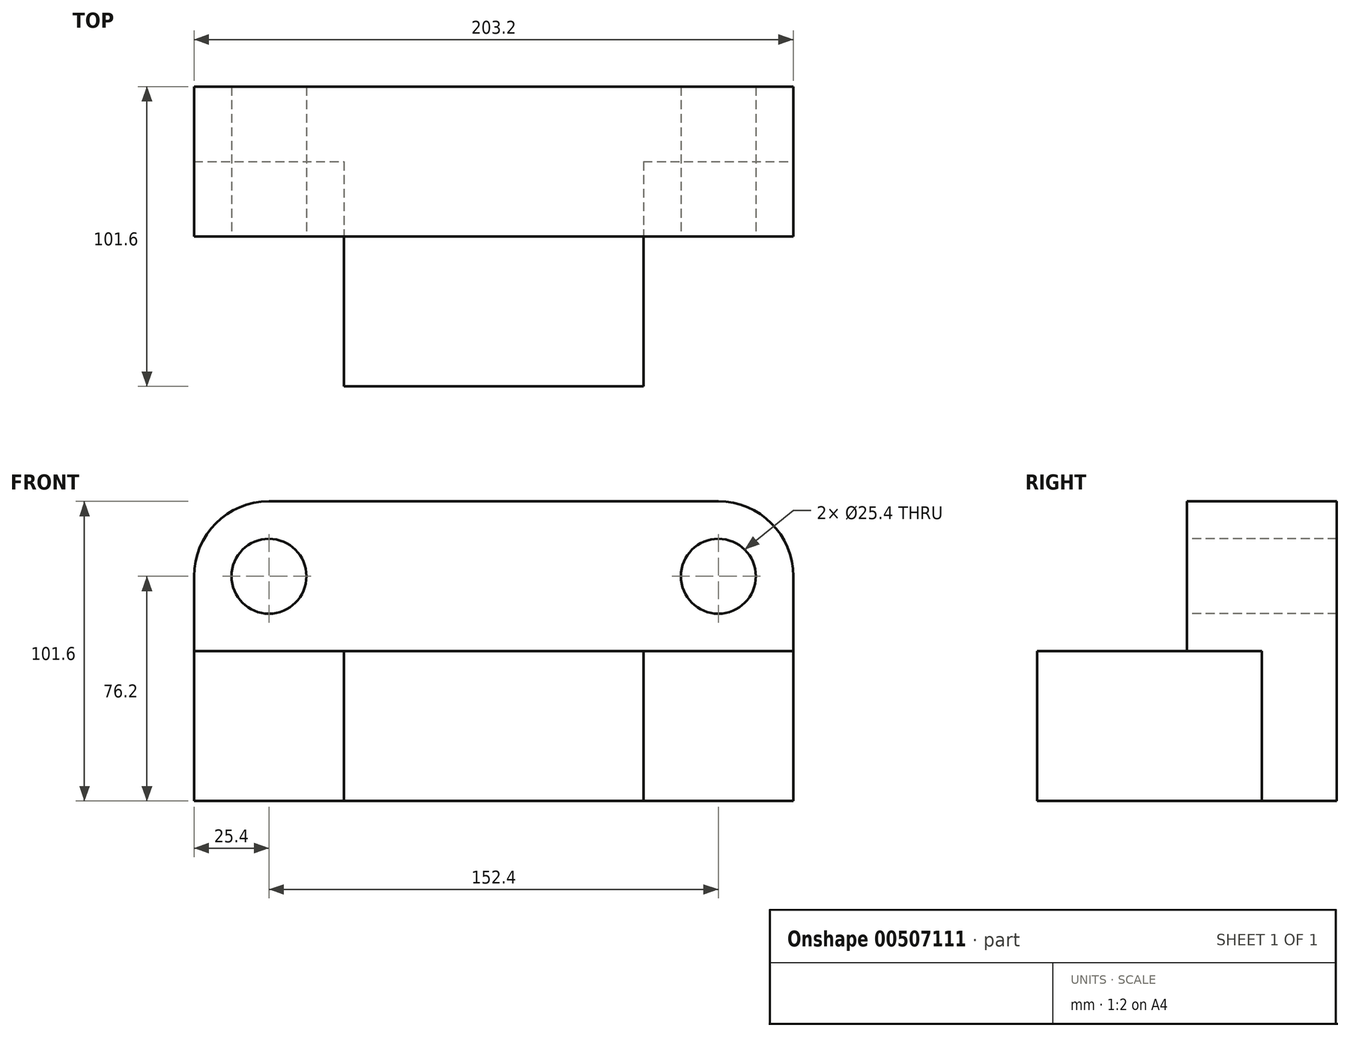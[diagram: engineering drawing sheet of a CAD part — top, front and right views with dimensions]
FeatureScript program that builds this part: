
annotation { "Feature Type Name" : "Feature", "Feature Type Description" : "" }
export const myFeature = defineFeature(function(context is Context, id is Id, definition is map)
    precondition{}
    {
        {
            var Q0;
            Q0=qCreatedBy(makeId("Front.planeOp"),FACE);
            var sketch = newSketch(context, id + "F0", { "sketchPlane" : qUnion([Q0])});
            skLineSegment(sketch, "E0", {"start": v(0, 0) * mm, "end": v(-101.6, 0) * mm});
            skLineSegment(sketch, "E1", {"start": v(-101.6, 0) * mm, "end": v(-101.6, 50.8) * mm});
            skLineSegment(sketch, "E2", {"start": v(-101.6, 50.8) * mm, "end": v(0, 50.8) * mm});
            skLineSegment(sketch, "E3", {"start": v(0, 50.8) * mm, "end": v(0, 0) * mm});
            skSolve(sketch);
        }
        {
            var Q0;
            Q0=makeQuery(id+"F0.imprint","IMPRINT",FACE,{"disambiguationData":[TD([[makeQuery(id+"F0.imprint","IMPRINT",EDGE,{"derivedFrom":sQuery(id+"F0.wireOp",EDGE,"E0")}),-1.0]])]});
            extrude(context, id + "F1", {"entities" : qUnion([Q0]), "oppositeDirection" : true, "depth" : 76.2 * mm});
        }
        {
            var Q0;
            Q0=makeQuery(id+"F1.opExtrude","CAP_FACE",FACE,{"disambiguationData":[OSD([sQuery(id+"F0.wireOp",EDGE,"E0"),sQuery(id+"F0.wireOp",EDGE,"E1"),sQuery(id+"F0.wireOp",EDGE,"E2"),sQuery(id+"F0.wireOp",EDGE,"E3")])],"isStart":false});
            var sketch = newSketch(context, id + "F2", { "sketchPlane" : qUnion([Q0])});
            skLineSegment(sketch, "E4", {"start": v(0, 0) * mm, "end": v(-50.8, 0) * mm});
            skLineSegment(sketch, "E5", {"start": v(-50.8, 0) * mm, "end": v(-50.8, 50.8) * mm});
            skLineSegment(sketch, "E6", {"start": v(-50.8, 50.8) * mm, "end": v(152.4, 50.8) * mm});
            skLineSegment(sketch, "E7", {"start": v(152.4, 50.8) * mm, "end": v(152.4, 0) * mm});
            skLineSegment(sketch, "E8", {"start": v(152.4, 0) * mm, "end": v(0, 0) * mm});
            skSolve(sketch);
        }
        {
            var Q0;
            Q0=makeQuery(id+"F2.imprint","IMPRINT",FACE,{"disambiguationData":[TD([[makeQuery(id+"F2.imprint","IMPRINT",EDGE,{"derivedFrom":sQuery(id+"F2.wireOp",EDGE,"E4")}),-1.0]])]});
            var Q1;
            {var subQ1=makeQuery(id+"F1.opExtrude","CAP_EDGE",EDGE,{"disambiguationData":[OSD([sQuery(id+"F0.wireOp",EDGE,"E1")])],"isStart":false});Q1=makeQuery(id+"F2.imprint","IMPRINT",FACE,{"disambiguationData":[TD([[makeQuery(id+"F2.imprint","IMPRINT",EDGE,{"derivedFrom":subQ1}),1.0]])]});}
            var Q2;
            {var subQ2=sQuery(id+"F2.wireOp",EDGE,"E7");Q2=makeQuery(id+"F2.imprint","IMPRINT",FACE,{"disambiguationData":[TD([[makeQuery(id+"F2.imprint","IMPRINT",EDGE,{"derivedFrom":subQ2}),-1.0]])]});}
            extrude(context, id + "F3", {"entities" : qUnion([Q0, Q1, Q2]), "operationType" : NewBodyOperationType.ADD, "depth" : 25.4 * mm});
        }
        {
            var Q0;
            Q0=makeQuery(id+"F3.boolean.opBoolean","MERGE",FACE,{"derivedFrom":[makeQuery(id+"F1.opExtrude","SWEPT_FACE",FACE,{"disambiguationData":[OSD([sQuery(id+"F0.wireOp",EDGE,"E2")])]}),makeQuery(id+"F3.opExtrude","SWEPT_FACE",FACE,{"disambiguationData":[OSD([sQuery(id+"F2.wireOp",EDGE,"E6")])]})]});
            var sketch = newSketch(context, id + "F4", { "sketchPlane" : qUnion([Q0])});
            skLineSegment(sketch, "E9", {"start": v(50.8, 101.6) * mm, "end": v(50.8, 50.8) * mm});
            skLineSegment(sketch, "E10", {"start": v(50.8, 50.8) * mm, "end": v(-152.4, 50.8) * mm});
            skLineSegment(sketch, "E11", {"start": v(-152.4, 50.8) * mm, "end": v(-152.4, 101.6) * mm});
            skLineSegment(sketch, "E12", {"start": v(-152.4, 101.6) * mm, "end": v(50.8, 101.6) * mm});
            skSolve(sketch);
        }
        {
            var Q0;
            {var subQ0=sQuery(id+"F4.wireOp",EDGE,"E11");var subQ1=sQuery(id+"F4.wireOp",EDGE,"E10");var subQ2=makeQuery(id+"F4.imprint","INTERSECT",VERTEX,{"derivedFrom":[subQ1,subQ0]});Q0=makeQuery(id+"F4.imprint","IMPRINT",FACE,{"disambiguationData":[TD([[makeQuery(id+"F4.imprint","IMPRINT",EDGE,{"disambiguationData":[TD([[subQ2,1.0]])],"derivedFrom":subQ1}),-1.0]])]});}
            var Q1;
            {var subQ0=sQuery(id+"F4.wireOp",EDGE,"E12");Q1=makeQuery(id+"F4.imprint","IMPRINT",FACE,{"disambiguationData":[TD([[makeQuery(id+"F4.imprint","IMPRINT",EDGE,{"derivedFrom":subQ0}),1.0]])]});}
            var Q2;
            {var subQ0=sQuery(id+"F4.wireOp",EDGE,"E9");var subQ6=sQuery(id+"F4.wireOp",EDGE,"E10");var subQ7=makeQuery(id+"F4.imprint","INTERSECT",VERTEX,{"derivedFrom":[subQ0,subQ6]});Q2=makeQuery(id+"F4.imprint","IMPRINT",FACE,{"disambiguationData":[TD([[makeQuery(id+"F4.imprint","IMPRINT",EDGE,{"disambiguationData":[TD([[subQ7,-1.0]])],"derivedFrom":subQ6}),-1.0]])]});}
            extrude(context, id + "F5", {"entities" : qUnion([Q0, Q1, Q2]), "operationType" : NewBodyOperationType.ADD, "depth" : 50.8 * mm});
        }
        {
            var Q0;
            Q0=makeQuery(id+"F5.opExtrude","CAP_EDGE",EDGE,{"disambiguationData":[OSD([sQuery(id+"F4.wireOp",EDGE,"E9")])],"isStart":false});
            fillet(context, id + "F6", {"entities" : qUnion([Q0]), "radius" : 25.4 * mm, "tangentPropagation" : true, "allowEdgeOverflow" : false});
        }
        {
            var Q0;
            Q0=makeQuery(id+"F5.opExtrude","CAP_EDGE",EDGE,{"disambiguationData":[OSD([sQuery(id+"F4.wireOp",EDGE,"E11")])],"isStart":false});
            fillet(context, id + "F7", {"entities" : qUnion([Q0]), "radius" : 25.4 * mm, "tangentPropagation" : true, "allowEdgeOverflow" : false});
        }
        {
            var Q0;
            Q0=makeQuery(id+"F5.opExtrude","SWEPT_FACE",FACE,{"disambiguationData":[OSD([sQuery(id+"F4.wireOp",EDGE,"E10")])]});
            var sketch = newSketch(context, id + "F8", { "sketchPlane" : qUnion([Q0])});
            skCircle(sketch, "E13", {"center": v(-127, 76.2) * mm, "radius": 12.7 * mm});
            skCircle(sketch, "E14", {"center": v(25.4, 76.2) * mm, "radius": 12.7 * mm});
            skSolve(sketch);
        }
        {
            var Q0;
            Q0=makeQuery(id+"F8.imprint","IMPRINT",FACE,{"disambiguationData":[TD([[makeQuery(id+"F8.imprint","IMPRINT",EDGE,{"derivedFrom":sQuery(id+"F8.wireOp",EDGE,"E13")}),1.0]])]});
            var Q1;
            Q1=makeQuery(id+"F8.imprint","IMPRINT",FACE,{"disambiguationData":[TD([[makeQuery(id+"F8.imprint","IMPRINT",EDGE,{"derivedFrom":sQuery(id+"F8.wireOp",EDGE,"E14")}),1.0]])]});
            extrude(context, id + "F9", {"entities" : qUnion([Q0, Q1]), "operationType" : NewBodyOperationType.REMOVE, "oppositeDirection" : true, "depth" : 50.8 * mm});
        }
    });
